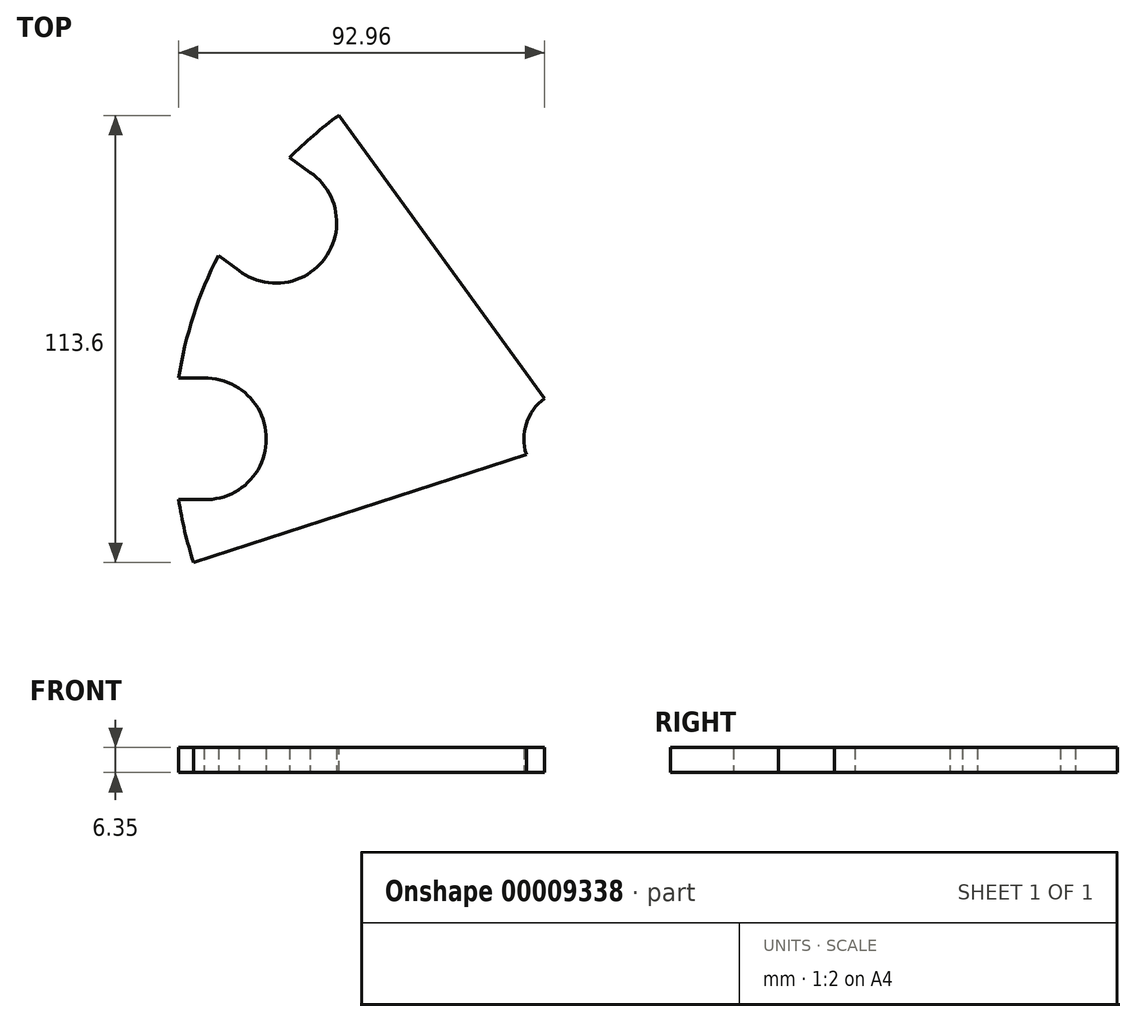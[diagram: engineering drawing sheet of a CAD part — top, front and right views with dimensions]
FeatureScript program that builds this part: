
annotation { "Feature Type Name" : "Feature", "Feature Type Description" : "" }
export const myFeature = defineFeature(function(context is Context, id is Id, definition is map)
    precondition{}
    {
        {
            var Q0;
            Q0=qCreatedBy(makeId("Top.planeOp"),FACE);
            var sketch = newSketch(context, id + "F0", { "sketchPlane" : qUnion([Q0])});
            skArc(sketch, "E0", {"start": v(100.42, 15.42) * mm, "mid": v(96.63, 31.4) * mm, "end": v(90.3, 46.55) * mm});
            skArc(sketch, "E1", {"start": v(94, 15.42) * mm, "mid": v(78.14, 0) * mm, "end": v(94, -15.42) * mm});
            skLineSegment(sketch, "E2", {"start": v(94, 15.42) * mm, "end": v(100.42, 15.42) * mm});
            skLineSegment(sketch, "E3", {"start": v(94, -15.42) * mm, "end": v(100.42, -15.42) * mm});
            skLineSegment(sketch, "E4.1.0", {"start": v(66.98, 67.73) * mm, "end": v(72.18, 71.5) * mm});
            skArc(sketch, "E4.1.1", {"start": v(66.98, 67.73) * mm, "mid": v(63.22, 45.93) * mm, "end": v(85.1, 42.77) * mm});
            skLineSegment(sketch, "E4.1.2", {"start": v(85.1, 42.77) * mm, "end": v(90.3, 46.55) * mm});
            skLineSegment(sketch, "E4.2.0", {"start": v(14.38, 94.16) * mm, "end": v(16.36, 100.27) * mm});
            skArc(sketch, "E4.2.1", {"start": v(14.38, 94.16) * mm, "mid": v(24.15, 74.32) * mm, "end": v(43.71, 84.63) * mm});
            skLineSegment(sketch, "E4.2.2", {"start": v(43.71, 84.63) * mm, "end": v(45.7, 90.74) * mm});
            skLineSegment(sketch, "E4.3.0", {"start": v(-43.71, 84.63) * mm, "end": v(-45.7, 90.74) * mm});
            skArc(sketch, "E4.3.1", {"start": v(-43.71, 84.63) * mm, "mid": v(-24.15, 74.32) * mm, "end": v(-14.38, 94.16) * mm});
            skLineSegment(sketch, "E4.3.2", {"start": v(-14.38, 94.16) * mm, "end": v(-16.36, 100.27) * mm});
            skLineSegment(sketch, "E4.4.0", {"start": v(-85.1, 42.77) * mm, "end": v(-90.3, 46.55) * mm});
            skArc(sketch, "E4.4.1", {"start": v(-85.1, 42.77) * mm, "mid": v(-63.22, 45.93) * mm, "end": v(-66.98, 67.73) * mm});
            skLineSegment(sketch, "E4.4.2", {"start": v(-66.98, 67.73) * mm, "end": v(-72.18, 71.5) * mm});
            skLineSegment(sketch, "E4.5.0", {"start": v(-94, -15.42) * mm, "end": v(-100.42, -15.42) * mm});
            skArc(sketch, "E4.5.1", {"start": v(-94, -15.42) * mm, "mid": v(-78.14, 0) * mm, "end": v(-94, 15.42) * mm});
            skLineSegment(sketch, "E4.5.2", {"start": v(-94, 15.42) * mm, "end": v(-100.42, 15.42) * mm});
            skLineSegment(sketch, "E4.6.0", {"start": v(-66.98, -67.73) * mm, "end": v(-72.18, -71.5) * mm});
            skArc(sketch, "E4.6.1", {"start": v(-66.98, -67.73) * mm, "mid": v(-63.22, -45.93) * mm, "end": v(-85.1, -42.77) * mm});
            skLineSegment(sketch, "E4.6.2", {"start": v(-85.1, -42.77) * mm, "end": v(-90.3, -46.55) * mm});
            skLineSegment(sketch, "E4.7.0", {"start": v(-14.38, -94.16) * mm, "end": v(-16.36, -100.27) * mm});
            skArc(sketch, "E4.7.1", {"start": v(-14.38, -94.16) * mm, "mid": v(-24.15, -74.32) * mm, "end": v(-43.71, -84.63) * mm});
            skLineSegment(sketch, "E4.7.2", {"start": v(-43.71, -84.63) * mm, "end": v(-45.7, -90.74) * mm});
            skLineSegment(sketch, "E4.8.0", {"start": v(43.71, -84.63) * mm, "end": v(45.7, -90.74) * mm});
            skArc(sketch, "E4.8.1", {"start": v(43.71, -84.63) * mm, "mid": v(24.15, -74.32) * mm, "end": v(14.38, -94.16) * mm});
            skLineSegment(sketch, "E4.8.2", {"start": v(14.38, -94.16) * mm, "end": v(16.36, -100.27) * mm});
            skLineSegment(sketch, "E4.9.0", {"start": v(85.1, -42.77) * mm, "end": v(90.3, -46.55) * mm});
            skArc(sketch, "E4.9.1", {"start": v(85.1, -42.77) * mm, "mid": v(63.22, -45.93) * mm, "end": v(66.98, -67.73) * mm});
            skLineSegment(sketch, "E4.9.2", {"start": v(66.98, -67.73) * mm, "end": v(72.18, -71.5) * mm});
            skArc(sketch, "E5.trimOffspring", {"start": v(-90.3, 46.55) * mm, "mid": v(-96.63, 31.4) * mm, "end": v(-100.42, 15.42) * mm});
            skArc(sketch, "E6.trimOffspring", {"start": v(-45.7, 90.74) * mm, "mid": v(-59.72, 82.2) * mm, "end": v(-72.18, 71.5) * mm});
            skArc(sketch, "E7.trimOffspring", {"start": v(16.36, 100.27) * mm, "mid": v(0, 101.6) * mm, "end": v(-16.36, 100.27) * mm});
            skArc(sketch, "E8.trimOffspring", {"start": v(72.18, 71.5) * mm, "mid": v(59.72, 82.2) * mm, "end": v(45.7, 90.74) * mm});
            skArc(sketch, "E9.trimOffspring", {"start": v(90.3, -46.55) * mm, "mid": v(96.63, -31.4) * mm, "end": v(100.42, -15.42) * mm});
            skArc(sketch, "E10.trimOffspring", {"start": v(45.7, -90.74) * mm, "mid": v(59.72, -82.2) * mm, "end": v(72.18, -71.5) * mm});
            skArc(sketch, "E11.trimOffspring", {"start": v(-16.36, -100.27) * mm, "mid": v(0, -101.6) * mm, "end": v(16.36, -100.27) * mm});
            skArc(sketch, "E12.trimOffspring", {"start": v(-72.18, -71.5) * mm, "mid": v(-59.72, -82.2) * mm, "end": v(-45.7, -90.74) * mm});
            skArc(sketch, "E13.trimOffspring", {"start": v(-100.42, -15.42) * mm, "mid": v(-96.63, -31.4) * mm, "end": v(-90.3, -46.55) * mm});
            skCircle(sketch, "E14", {"center": v(0, 0) * mm, "radius": 12.7 * mm});
            skSolve(sketch);
        }
        {
            var Q0;
            Q0=makeQuery(id+"F0.imprint","IMPRINT",FACE,{"disambiguationData":[TD([[makeQuery(id+"F0.imprint","IMPRINT",EDGE,{"derivedFrom":sQuery(id+"F0.wireOp",EDGE,"E0")}),1.0]])]});
            extrude(context, id + "F1", {"entities" : qUnion([Q0]), "depth" : 6.35 * mm});
        }
        {
            var Q0;
            Q0=makeQuery(id+"F1.opExtrude","CAP_FACE",FACE,{"disambiguationData":[OSD([sQuery(id+"F0.wireOp",EDGE,"E0"),sQuery(id+"F0.wireOp",EDGE,"E1"),sQuery(id+"F0.wireOp",EDGE,"E2"),sQuery(id+"F0.wireOp",EDGE,"E3"),sQuery(id+"F0.wireOp",EDGE,"E4.1.0"),sQuery(id+"F0.wireOp",EDGE,"E4.1.1"),sQuery(id+"F0.wireOp",EDGE,"E4.1.2"),sQuery(id+"F0.wireOp",EDGE,"E4.2.0"),sQuery(id+"F0.wireOp",EDGE,"E4.2.1"),sQuery(id+"F0.wireOp",EDGE,"E4.2.2"),sQuery(id+"F0.wireOp",EDGE,"E4.3.0"),sQuery(id+"F0.wireOp",EDGE,"E4.3.1"),sQuery(id+"F0.wireOp",EDGE,"E4.3.2"),sQuery(id+"F0.wireOp",EDGE,"E4.4.0"),sQuery(id+"F0.wireOp",EDGE,"E4.4.1"),sQuery(id+"F0.wireOp",EDGE,"E4.4.2"),sQuery(id+"F0.wireOp",EDGE,"E4.5.0"),sQuery(id+"F0.wireOp",EDGE,"E4.5.1"),sQuery(id+"F0.wireOp",EDGE,"E4.5.2"),sQuery(id+"F0.wireOp",EDGE,"E4.6.0"),sQuery(id+"F0.wireOp",EDGE,"E4.6.1"),sQuery(id+"F0.wireOp",EDGE,"E4.6.2"),sQuery(id+"F0.wireOp",EDGE,"E4.7.0"),sQuery(id+"F0.wireOp",EDGE,"E4.7.1"),sQuery(id+"F0.wireOp",EDGE,"E4.7.2"),sQuery(id+"F0.wireOp",EDGE,"E4.8.0"),sQuery(id+"F0.wireOp",EDGE,"E4.8.1"),sQuery(id+"F0.wireOp",EDGE,"E4.8.2"),sQuery(id+"F0.wireOp",EDGE,"E4.9.0"),sQuery(id+"F0.wireOp",EDGE,"E4.9.1"),sQuery(id+"F0.wireOp",EDGE,"E4.9.2"),sQuery(id+"F0.wireOp",EDGE,"E5.trimOffspring"),sQuery(id+"F0.wireOp",EDGE,"E6.trimOffspring"),sQuery(id+"F0.wireOp",EDGE,"E7.trimOffspring"),sQuery(id+"F0.wireOp",EDGE,"E8.trimOffspring"),sQuery(id+"F0.wireOp",EDGE,"E9.trimOffspring"),sQuery(id+"F0.wireOp",EDGE,"E10.trimOffspring"),sQuery(id+"F0.wireOp",EDGE,"E11.trimOffspring"),sQuery(id+"F0.wireOp",EDGE,"E12.trimOffspring"),sQuery(id+"F0.wireOp",EDGE,"E13.trimOffspring"),sQuery(id+"F0.wireOp",EDGE,"E14")])],"isStart":false});
            var sketch = newSketch(context, id + "F2", { "sketchPlane" : qUnion([Q0])});
            skLineSegment(sketch, "E15", {"start": v(0, 0) * mm, "end": v(59.72, 82.2) * mm});
            skLineSegment(sketch, "E16", {"start": v(0, 0) * mm, "end": v(-96.63, -31.4) * mm});
            skLineSegment(sketch, "E17", {"start": v(0, 0) * mm, "end": v(96.63, -31.4) * mm});
            skLineSegment(sketch, "E18", {"start": v(0, 0) * mm, "end": v(0, -101.6) * mm});
            skLineSegment(sketch, "E19", {"start": v(0, 0) * mm, "end": v(-59.72, 82.2) * mm});
            skSolve(sketch);
        }
        {
            var Q0;
            Q0=makeQuery(id+"F2.imprint","IMPRINT",FACE,{"disambiguationData":[TD([[makeQuery(id+"F2.imprint","IMPRINT",EDGE,{"derivedFrom":makeQuery(id+"F1.opExtrude","CAP_EDGE",EDGE,{"disambiguationData":[OSD([sQuery(id+"F0.wireOp",EDGE,"E4.2.0")])],"isStart":false})}),1.0]])]});
            var Q1;
            Q1=makeQuery(id+"F2.imprint","IMPRINT",FACE,{"disambiguationData":[TD([[makeQuery(id+"F2.imprint","IMPRINT",EDGE,{"derivedFrom":makeQuery(id+"F1.opExtrude","CAP_EDGE",EDGE,{"disambiguationData":[OSD([sQuery(id+"F0.wireOp",EDGE,"E0")])],"isStart":false})}),1.0]])]});
            var Q2;
            Q2=makeQuery(id+"F2.imprint","IMPRINT",FACE,{"disambiguationData":[TD([[makeQuery(id+"F2.imprint","IMPRINT",EDGE,{"derivedFrom":makeQuery(id+"F1.opExtrude","CAP_EDGE",EDGE,{"disambiguationData":[OSD([sQuery(id+"F0.wireOp",EDGE,"E4.8.0")])],"isStart":false})}),1.0]])]});
            var Q3;
            Q3=makeQuery(id+"F2.imprint","IMPRINT",FACE,{"disambiguationData":[TD([[makeQuery(id+"F2.imprint","IMPRINT",EDGE,{"derivedFrom":makeQuery(id+"F1.opExtrude","CAP_EDGE",EDGE,{"disambiguationData":[OSD([sQuery(id+"F0.wireOp",EDGE,"E4.6.0")])],"isStart":false})}),1.0]])]});
            extrude(context, id + "F3", {"entities" : qUnion([Q0, Q1, Q2, Q3]), "operationType" : NewBodyOperationType.REMOVE, "oppositeDirection" : true, "depth" : 25.4 * mm});
        }
    });
